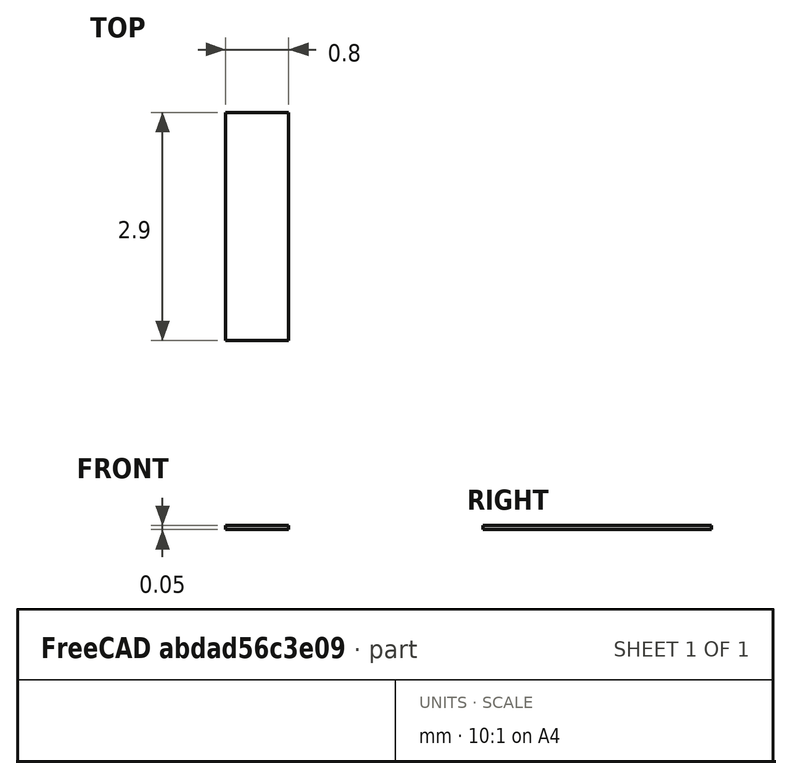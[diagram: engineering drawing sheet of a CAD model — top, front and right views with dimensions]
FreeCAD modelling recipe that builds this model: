
FCSTD DOCUMENT  (FreeCAD 0.17R12607 (Git))
Label: MicroSD Card Short Pin
License: All rights reserved
LicenseURL: http://en.wikipedia.org/wiki/All_rights_reserved
objects: Sketcher::SketchObject×1, PartDesign::Pad×1, PartDesign::Body×1
note: 4 computed .brp shape members not serialized (recipe doc carries the construction recipe); baked Part::Feature solids carry a one-line shape summary decoded from their .brp

FEATURE [Sketcher::SketchObject] Sketch  label="Pin Sketch"
  MapMode = 5
  Support = -> [XY_Plane]
  sketch-geometry (4):
    g0: LineSegment StartX=-0.4 StartY=-1.45 StartZ=0 EndX=0.4 EndY=-1.45 EndZ=0
    g1: LineSegment StartX=0.4 StartY=-1.45 StartZ=0 EndX=0.4 EndY=1.45 EndZ=0
    g2: LineSegment StartX=0.4 StartY=1.45 StartZ=0 EndX=-0.4 EndY=1.45 EndZ=0
    g3: LineSegment StartX=-0.4 StartY=1.45 StartZ=0 EndX=-0.4 EndY=-1.45 EndZ=0
  constraints (12):
    c: Coincident(g0,g1)
    c: Coincident(g1,g2)
    c: Coincident(g2,g3)
    c: Coincident(g3,g0)
    c: Horizontal(g0)
    c: Horizontal(g2)
    c: Vertical(g1)
    c: Vertical(g3)
    c: DistanceX(g2,g2) = 0.8
    c: DistanceY(g1,g1) = 2.9
    c: Symmetric(g2,g1,g-2)
    c: Symmetric(g1,g0,g-1)
FEATURE [PartDesign::Pad] Pad  label="Pin"
  Length = 0.05
  Length2 = 100
  Profile = -> Sketch
  Type = 0
FEATURE [PartDesign::Body] Body
  Group = -> [Sketch,Pad]
  Origin = -> Origin
  Tip = -> Pad
